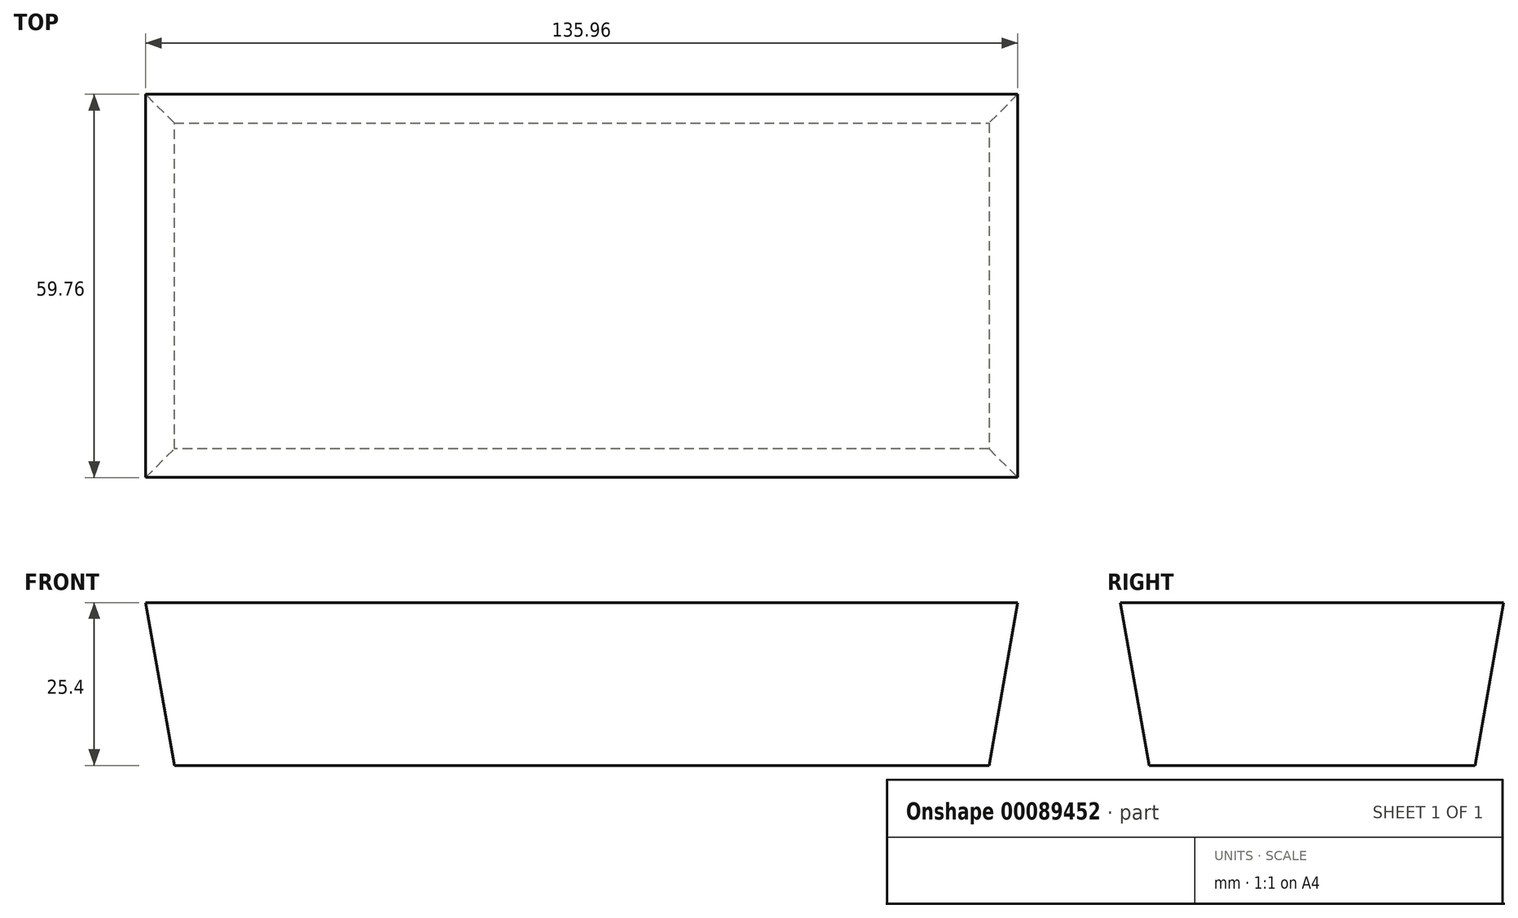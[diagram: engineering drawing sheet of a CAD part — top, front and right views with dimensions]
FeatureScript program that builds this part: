
annotation { "Feature Type Name" : "Feature", "Feature Type Description" : "" }
export const myFeature = defineFeature(function(context is Context, id is Id, definition is map)
    precondition{}
    {
        {
            var Q0;
            Q0=qCreatedBy(makeId("Top.planeOp"),FACE);
            var sketch = newSketch(context, id + "F0", { "sketchPlane" : qUnion([Q0])});
            skLineSegment(sketch, "E0.bottom", {"start": v(-45.01, 22.33) * mm, "end": v(81.99, 22.33) * mm});
            skLineSegment(sketch, "E0.top", {"start": v(-45.01, -28.47) * mm, "end": v(81.99, -28.47) * mm});
            skLineSegment(sketch, "E0.left", {"start": v(-45.01, 22.33) * mm, "end": v(-45.01, -28.47) * mm});
            skLineSegment(sketch, "E0.right", {"start": v(81.99, 22.33) * mm, "end": v(81.99, -28.47) * mm});
            skSolve(sketch);
        }
        {
            var Q0;
            Q0=makeQuery(id+"F0.imprint","IMPRINT",FACE,{"disambiguationData":[TD([[makeQuery(id+"F0.imprint","IMPRINT",EDGE,{"derivedFrom":sQuery(id+"F0.wireOp",EDGE,"E0.bottom")}),-1.0]])]});
            extrude(context, id + "F1", {"entities" : qUnion([Q0]), "depth" : 25.4 * mm, "hasDraft" : true, "draftAngle" : 10 * degree});
        }
    });
